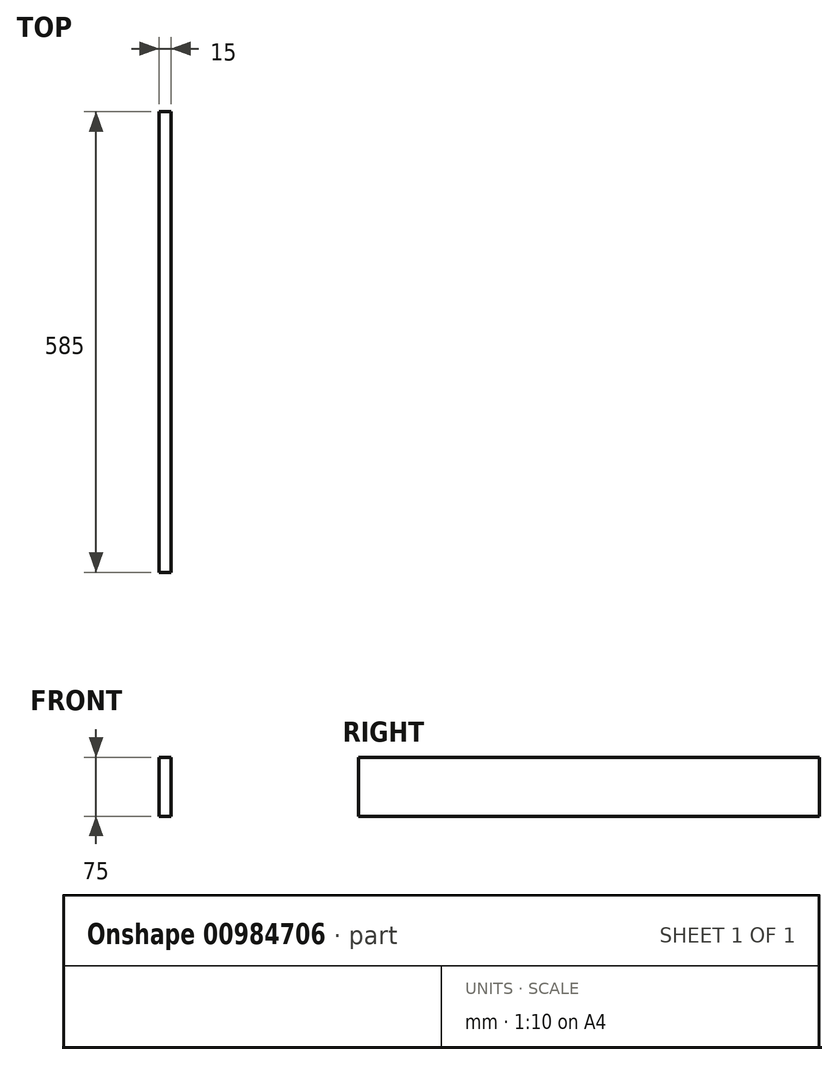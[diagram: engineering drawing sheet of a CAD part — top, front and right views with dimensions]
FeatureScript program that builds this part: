
annotation { "Feature Type Name" : "Feature", "Feature Type Description" : "" }
export const myFeature = defineFeature(function(context is Context, id is Id, definition is map)
    precondition{}
    {
        {
            var Q0;
            Q0=qCreatedBy(makeId("Front.planeOp"),FACE);
            var sketch = newSketch(context, id + "F0", { "sketchPlane" : qUnion([Q0])});
            skLineSegment(sketch, "E0.bottom", {"start": v(-140.78, 55.26) * mm, "end": v(-125.78, 55.26) * mm});
            skLineSegment(sketch, "E0.top", {"start": v(-140.78, -19.74) * mm, "end": v(-125.78, -19.74) * mm});
            skLineSegment(sketch, "E0.left", {"start": v(-140.78, 55.26) * mm, "end": v(-140.78, -19.74) * mm});
            skLineSegment(sketch, "E0.right", {"start": v(-125.78, 55.26) * mm, "end": v(-125.78, -19.74) * mm});
            skSolve(sketch);
        }
        {
            var Q0;
            Q0=makeQuery(id+"F0.imprint","IMPRINT",FACE,{"disambiguationData":[TD([[makeQuery(id+"F0.imprint","IMPRINT",EDGE,{"derivedFrom":sQuery(id+"F0.wireOp",EDGE,"E0.bottom")}),-1.0]])]});
            extrude(context, id + "F1", {"entities" : qUnion([Q0]), "depth" : 585 * mm, "offsetDistance" : 25 * mm});
        }
    });
